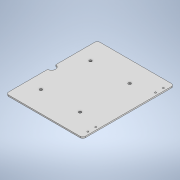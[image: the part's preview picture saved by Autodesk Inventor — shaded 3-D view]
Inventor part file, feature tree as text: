
AUTODESK INVENTOR PART (.ipt)
format: ipt  version: 2021 (Build 250183000, 183)  size: 162,304 bytes
history: native  units: mm
features: sketch x5, extrude x3, fillet x3, hole x2, other x1, projected_geometry x1
ambient origin geometry x8: Origin, YZ Plane, XZ Plane, XY Plane, X Axis, Y Axis, Z Axis, Center Point
bodies: Body1 (feature_tree)
feature tree (15):
  other  "實體1"
  extrude  "擠出1"  Depth=294.0mm
  hole  "孔1"  [1 undecoded]
  fillet  "圓角1"  Radius=5.0mm
  hole  "孔2"  [1 undecoded]
  extrude  "擠出3"  Depth=30.0mm
  fillet  "圓角3"  Radius=10.5mm
  extrude  "擠出2"  Depth=229.0mm
  fillet  "圓角2"  Radius=10.0mm
  sketch  "草圖1"
  sketch  "草圖2"
  sketch  "草圖3"
  projected_geometry  "投影迴路1"
  sketch  "草圖4"
  sketch  "草圖5"
note: 2 required parameter values undecoded (feature->parameter linkage not recoverable at this tier; creation-order binding heuristic only, values carry confidence <= 0.55)
